# Revit family: Ventüer_VentilationLouvres_VL-VF2
name_source: partatom
category: Generic Models
units: mm (PartAtom-declared; Revit-internal decimal feet)

## family parameters
Always vertical = No
Can host rebar = No
Cut with Voids When Loaded = Yes
Part Type = Normal
Room Calculation Point = No
Round Connector Dimension = Use Diameter
Shared = No
Work Plane-Based = Yes

## types (2) — shared parameters
Aerodynamic Performance = Air Inlet: 0.317, Class 2. Air Extract: 0.317, Class 2
Ancillaries = Bird Mesh,Insect Mesh, Solid Blanking, Perimeter Mounting Angle
Blade And Frame Gap = 10 mm  [stored 0.0328084 ft]
Blade Centres = 50 mm  [stored 0.164042 ft]
Blade Horizontal Offset = 8 mm  [stored 0.0262467 ft]
Blade Material = Ventüer Aluminium
Default Elevation = 1219 mm
Description = Vertical Blade Louvre
Exact Neck Height = 594 mm  [stored 1.94882 ft]
Exact Neck Height Check = 594 mm  [stored 1.94882 ft]
Exact Neck Width = 594 mm  [stored 1.94882 ft]
Exact Neck Width Check = 594 mm  [stored 1.94882 ft]
Frame Material = Ventüer Aluminium
Frame Set Count = 1
Frame Set Count Check = 2
Frame Set Transition Count = 1
Frame Set Transition Count Check = 2
Manufacturer = Ventüer
Max Flow = 5000.0 L/s
Min Flow = 100.0 L/s
Model = VL-VF2
Multiple Frame Set = No
Multiple Transition = No
Noise Level NC Max = 0.00 NC
Noise Level NC Min = 0.00 NC
Nominal Height = 600 mm  [stored 1.9685 ft]
Nominal Width = 600 mm  [stored 1.9685 ft]
Nominated Air Flow = 100.0 L/s
Nominated Pessure Drop = 21.0 Pa
Rain Defence Performance = Class A - up to 3.5m/s suction velocity
Single Frame Set = Yes
Single Transition = No
Specified Air Flow = 0.0 L/s
Specified Pressure Drop = 21.0 Pa
Static Pressure Max = 60.0 Pa
Static Pressure Min = 10.0 Pa
URL = https://www.ventuer.co
Ventüer Product Range = Ventilation Louvres
zero-valued in all types: End Blade Corrector

## per-type parameters (varying)
| type | Base Width | Blade Count | Blade Cut Offset | Connector Height | Connector Width | Depth | End Blade Width | Flanged | Frame Set Height | Glazed | Overall Opening Height | Overall Opening Width | Profile Width | Screen Symbol Distance | Siffener Length | Single Frame Set Height |
| VL-VF2_GF | 26 mm | 10 | 500 mm  [stored 1.64042 ft] | 542 mm  [stored 1.77822 ft] | 542 mm  [stored 1.77822 ft] | 105 mm  [stored 0.344488 ft] | 32 mm | No | 542 mm  [stored 1.77822 ft] | Yes | 542 mm  [stored 1.77822 ft] | 542 mm  [stored 1.77822 ft] | 26 mm | 6 mm  [stored 0.019685 ft] | 542 mm  [stored 1.77822 ft] | 271 mm  [stored 0.889108 ft] |
| VL-VF2_FF | 52 mm | 9 | 450 mm  [stored 1.47638 ft] | 490 mm  [stored 1.60761 ft] | 490 mm  [stored 1.60761 ft] | 101 mm | 30 mm  [stored 0.0984252 ft] | Yes | 490 mm  [stored 1.60761 ft] | No | 490 mm  [stored 1.60761 ft] | 490 mm  [stored 1.60761 ft] | 52 mm | 4 mm  [stored 0.0131234 ft] | 490 mm  [stored 1.60761 ft] | 245 mm  [stored 0.803806 ft] |

note: column(s) folded — value = type name in every type: Keynote

note: [stored X ft] marks values corroborated as IEEE doubles in the binary element streams (Revit-internal decimal feet)

## geometry (parser evidence)
native form markers: Extrusion x1, Sweep x34
no freeform markers — native parametric forms only
